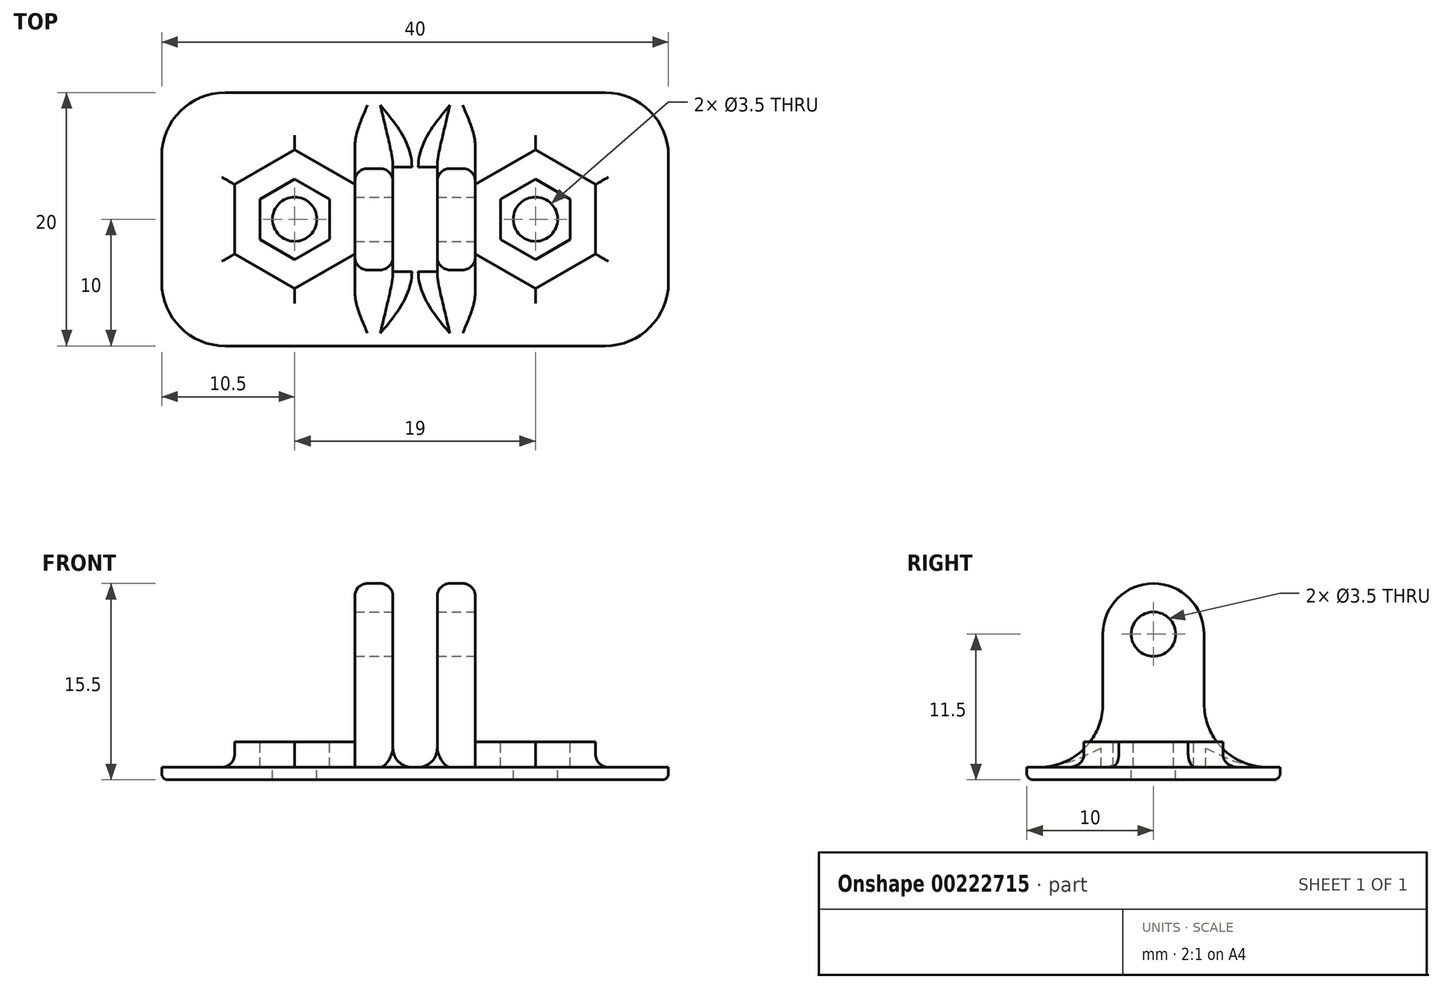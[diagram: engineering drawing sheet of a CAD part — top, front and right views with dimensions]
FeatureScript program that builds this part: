
annotation { "Feature Type Name" : "Feature", "Feature Type Description" : "" }
export const myFeature = defineFeature(function(context is Context, id is Id, definition is map)
    precondition{}
    {
        {
            var Q0;
            Q0=qCreatedBy(makeId("Top.planeOp"),FACE);
            var sketch = newSketch(context, id + "F0", { "sketchPlane" : qUnion([Q0])});
            skLineSegment(sketch, "E0.bottom", {"start": v(0, 0) * mm, "end": v(40, 0) * mm});
            skLineSegment(sketch, "E0.top", {"start": v(0, 20) * mm, "end": v(40, 20) * mm});
            skLineSegment(sketch, "E0.left", {"start": v(0, 0) * mm, "end": v(0, 20) * mm});
            skLineSegment(sketch, "E0.right", {"start": v(40, 0) * mm, "end": v(40, 20) * mm});
            skSolve(sketch);
        }
        {
            var Q0;
            Q0=makeQuery(id+"F0.imprint","IMPRINT",FACE,{"disambiguationData":[TD([[makeQuery(id+"F0.imprint","IMPRINT",EDGE,{"derivedFrom":sQuery(id+"F0.wireOp",EDGE,"E0.bottom")}),1.0]])]});
            extrude(context, id + "F1", {"entities" : qUnion([Q0]), "depth" : 3 * mm});
        }
        {
            var Q0;
            Q0=makeQuery(id+"F1.opExtrude","CAP_FACE",FACE,{"disambiguationData":[OSD([sQuery(id+"F0.wireOp",EDGE,"E0.bottom"),sQuery(id+"F0.wireOp",EDGE,"E0.top"),sQuery(id+"F0.wireOp",EDGE,"E0.left"),sQuery(id+"F0.wireOp",EDGE,"E0.right")])],"isStart":false});
            var sketch = newSketch(context, id + "F2", { "sketchPlane" : qUnion([Q0])});
            skLineSegment(sketch, "E1", {"start": v(20, 20) * mm, "end": v(20, 0) * mm, "construction": true});
            skLineSegment(sketch, "E2.bottom", {"start": v(15.25, 14) * mm, "end": v(18.25, 14) * mm});
            skLineSegment(sketch, "E2.top", {"start": v(15.25, 6) * mm, "end": v(18.25, 6) * mm});
            skLineSegment(sketch, "E2.left", {"start": v(15.25, 14) * mm, "end": v(15.25, 6) * mm});
            skLineSegment(sketch, "E2.right", {"start": v(18.25, 14) * mm, "end": v(18.25, 6) * mm});
            skLineSegment(sketch, "E3", {"start": v(0, 10) * mm, "end": v(40, 10) * mm, "construction": true});
            skLineSegment(sketch, "E4.MirrorCS", {"start": v(24.75, 6) * mm, "end": v(21.75, 6) * mm});
            skLineSegment(sketch, "E5.MirrorCS", {"start": v(40, 10) * mm, "end": v(0, 10) * mm, "construction": true});
            skLineSegment(sketch, "E6.MirrorCS", {"start": v(21.75, 14) * mm, "end": v(21.75, 6) * mm});
            skLineSegment(sketch, "E7.MirrorCS", {"start": v(24.75, 14) * mm, "end": v(24.75, 6) * mm});
            skLineSegment(sketch, "E8.MirrorCS", {"start": v(24.75, 14) * mm, "end": v(21.75, 14) * mm});
            skSolve(sketch);
        }
        {
            var Q0;
            Q0=makeQuery(id+"F2.imprint","IMPRINT",FACE,{"disambiguationData":[TD([[makeQuery(id+"F2.imprint","IMPRINT",EDGE,{"derivedFrom":sQuery(id+"F2.wireOp",EDGE,"E2.bottom")}),-1.0]])]});
            var Q1;
            Q1=makeQuery(id+"F2.imprint","IMPRINT",FACE,{"disambiguationData":[TD([[makeQuery(id+"F2.imprint","IMPRINT",EDGE,{"derivedFrom":sQuery(id+"F2.wireOp",EDGE,"E4.MirrorCS")}),-1.0]])]});
            extrude(context, id + "F3", {"entities" : qUnion([Q0, Q1]), "operationType" : NewBodyOperationType.ADD, "depth" : 12.5 * mm});
        }
        {
            var Q0;
            Q0=makeQuery(id+"F3.opExtrude","SWEPT_FACE",FACE,{"disambiguationData":[OSD([sQuery(id+"F2.wireOp",EDGE,"E7.MirrorCS")])]});
            var sketch = newSketch(context, id + "F4", { "sketchPlane" : qUnion([Q0])});
            skLineSegment(sketch, "E9", {"start": v(10, 15.5) * mm, "end": v(10, 3) * mm, "construction": true});
            skCircle(sketch, "E10", {"center": v(10, 11.5) * mm, "radius": 1.75 * mm});
            skSolve(sketch);
        }
        {
            var Q0;
            Q0=makeQuery(id+"F4.imprint","IMPRINT",FACE,{"disambiguationData":[TD([[makeQuery(id+"F4.imprint","IMPRINT",EDGE,{"derivedFrom":sQuery(id+"F4.wireOp",EDGE,"E10")}),1.0]])]});
            extrude(context, id + "F5", {"entities" : qUnion([Q0]), "operationType" : NewBodyOperationType.REMOVE, "endBound" : BoundingType.THROUGH_ALL, "oppositeDirection" : true, "depth" : 25 * mm});
        }
        {
            var Q0;
            Q0=makeQuery(id+"F1.opExtrude","CAP_FACE",FACE,{"disambiguationData":[OSD([sQuery(id+"F0.wireOp",EDGE,"E0.bottom"),sQuery(id+"F0.wireOp",EDGE,"E0.top"),sQuery(id+"F0.wireOp",EDGE,"E0.left"),sQuery(id+"F0.wireOp",EDGE,"E0.right")])],"isStart":false});
            var sketch = newSketch(context, id + "F6", { "sketchPlane" : qUnion([Q0])});
            skLineSegment(sketch, "E11.0.0", {"start": v(40, 20) * mm, "end": v(0, 20) * mm, "construction": true});
            skLineSegment(sketch, "E11.0.1", {"start": v(0, 20) * mm, "end": v(0, 0) * mm, "construction": true});
            skLineSegment(sketch, "E11.0.2", {"start": v(0, 0) * mm, "end": v(40, 0) * mm, "construction": true});
            skLineSegment(sketch, "E11.0.3", {"start": v(40, 0) * mm, "end": v(40, 20) * mm, "construction": true});
            skLineSegment(sketch, "E12", {"start": v(20, 20) * mm, "end": v(20, 0) * mm, "construction": true});
            skLineSegment(sketch, "E13", {"start": v(0, 10) * mm, "end": v(40.2, 10) * mm, "construction": true});
            skPoint(sketch, "E13.endSnap0", {"position": v(0, 10) * mm});
            skCircle(sketch, "E14.cCircle", {"center": v(20, 10) * mm, "radius": 8.23 * mm, "construction": true});
            skLineSegment(sketch, "E14.0", {"start": v(15.25, 18.23) * mm, "end": v(24.75, 18.23) * mm, "construction": true});
            skLineSegment(sketch, "E14.1", {"start": v(24.75, 18.23) * mm, "end": v(29.5, 10) * mm, "construction": true});
            skLineSegment(sketch, "E14.2", {"start": v(29.5, 10) * mm, "end": v(24.75, 1.77) * mm, "construction": true});
            skLineSegment(sketch, "E14.3", {"start": v(24.75, 1.77) * mm, "end": v(15.25, 1.77) * mm, "construction": true});
            skLineSegment(sketch, "E14.4", {"start": v(15.25, 1.77) * mm, "end": v(10.5, 10) * mm, "construction": true});
            skLineSegment(sketch, "E14.5", {"start": v(10.5, 10) * mm, "end": v(15.25, 18.23) * mm, "construction": true});
            skPoint(sketch, "E14.0.midPoint", {"position": v(20, 18.23) * mm});
            skCircle(sketch, "E15", {"center": v(10.5, 10) * mm, "radius": 1.75 * mm});
            skCircle(sketch, "E16", {"center": v(29.5, 10) * mm, "radius": 1.75 * mm});
            skSolve(sketch);
        }
        {
            var Q0;
            Q0 = qSketchRegion(id + "F6", true);
            extrude(context, id + "F7", {"entities" : qUnion([Q0]), "operationType" : NewBodyOperationType.REMOVE, "endBound" : BoundingType.THROUGH_ALL, "oppositeDirection" : true, "depth" : 25 * mm});
        }
        {
            var Q0;
            Q0=makeQuery(id+"F1.opExtrude","CAP_FACE",FACE,{"disambiguationData":[OSD([sQuery(id+"F0.wireOp",EDGE,"E0.bottom"),sQuery(id+"F0.wireOp",EDGE,"E0.top"),sQuery(id+"F0.wireOp",EDGE,"E0.left"),sQuery(id+"F0.wireOp",EDGE,"E0.right")])],"isStart":false});
            var sketch = newSketch(context, id + "F8", { "sketchPlane" : qUnion([Q0])});
            skCircle(sketch, "E17.cCircle", {"center": v(10.5, 10) * mm, "radius": 2.75 * mm, "construction": true});
            skLineSegment(sketch, "E17.0", {"start": v(13.25, 11.59) * mm, "end": v(13.25, 8.41) * mm});
            skLineSegment(sketch, "E17.1", {"start": v(13.25, 8.41) * mm, "end": v(10.5, 6.82) * mm});
            skLineSegment(sketch, "E17.2", {"start": v(10.5, 6.82) * mm, "end": v(7.75, 8.41) * mm});
            skLineSegment(sketch, "E17.3", {"start": v(7.75, 8.41) * mm, "end": v(7.75, 11.59) * mm});
            skLineSegment(sketch, "E17.4", {"start": v(7.75, 11.59) * mm, "end": v(10.5, 13.18) * mm});
            skLineSegment(sketch, "E17.5", {"start": v(10.5, 13.18) * mm, "end": v(13.25, 11.59) * mm});
            skPoint(sketch, "E17.0.midPoint", {"position": v(13.25, 10) * mm});
            skCircle(sketch, "E18.cCircle", {"center": v(29.5, 10) * mm, "radius": 2.75 * mm, "construction": true});
            skLineSegment(sketch, "E18.0", {"start": v(32.25, 11.59) * mm, "end": v(32.25, 8.41) * mm});
            skLineSegment(sketch, "E18.1", {"start": v(32.25, 8.41) * mm, "end": v(29.5, 6.82) * mm});
            skLineSegment(sketch, "E18.2", {"start": v(29.5, 6.82) * mm, "end": v(26.75, 8.41) * mm});
            skLineSegment(sketch, "E18.3", {"start": v(26.75, 8.41) * mm, "end": v(26.75, 11.59) * mm});
            skLineSegment(sketch, "E18.4", {"start": v(26.75, 11.59) * mm, "end": v(29.5, 13.18) * mm});
            skLineSegment(sketch, "E18.5", {"start": v(29.5, 13.18) * mm, "end": v(32.25, 11.59) * mm});
            skPoint(sketch, "E18.0.midPoint", {"position": v(32.25, 10) * mm});
            skLineSegment(sketch, "E19.0", {"start": v(0, 20) * mm, "end": v(40, 20) * mm});
            skLineSegment(sketch, "E19.1", {"start": v(0, 0) * mm, "end": v(0, 20) * mm});
            skLineSegment(sketch, "E19.2", {"start": v(0, 0) * mm, "end": v(40, 0) * mm});
            skLineSegment(sketch, "E19.3", {"start": v(40, 0) * mm, "end": v(40, 20) * mm});
            skCircle(sketch, "E20.cCircle", {"center": v(10.5, 10) * mm, "radius": 4.75 * mm, "construction": true});
            skPoint(sketch, "E20.cCircle.perimeterSnap0", {"position": v(18.25, 10) * mm});
            skLineSegment(sketch, "E20.0", {"start": v(15.25, 12.74) * mm, "end": v(15.25, 7.26) * mm});
            skLineSegment(sketch, "E20.1", {"start": v(15.25, 7.26) * mm, "end": v(10.5, 4.52) * mm});
            skLineSegment(sketch, "E20.2", {"start": v(10.5, 4.52) * mm, "end": v(5.75, 7.26) * mm});
            skLineSegment(sketch, "E20.3", {"start": v(5.75, 7.26) * mm, "end": v(5.75, 12.74) * mm});
            skLineSegment(sketch, "E20.4", {"start": v(5.75, 12.74) * mm, "end": v(10.5, 15.48) * mm});
            skLineSegment(sketch, "E20.5", {"start": v(10.5, 15.48) * mm, "end": v(15.25, 12.74) * mm});
            skPoint(sketch, "E20.0.midPoint", {"position": v(15.25, 10) * mm});
            skPoint(sketch, "E20.0.midPoint.positionSnap0", {"position": v(18.25, 10) * mm});
            skCircle(sketch, "E21.cCircle", {"center": v(29.5, 10) * mm, "radius": 4.75 * mm, "construction": true});
            skLineSegment(sketch, "E21.0", {"start": v(34.25, 12.74) * mm, "end": v(34.25, 7.26) * mm});
            skLineSegment(sketch, "E21.1", {"start": v(34.25, 7.26) * mm, "end": v(29.5, 4.52) * mm});
            skLineSegment(sketch, "E21.2", {"start": v(29.5, 4.52) * mm, "end": v(24.75, 7.26) * mm});
            skLineSegment(sketch, "E21.3", {"start": v(24.75, 7.26) * mm, "end": v(24.75, 12.74) * mm});
            skLineSegment(sketch, "E21.4", {"start": v(24.75, 12.74) * mm, "end": v(29.5, 15.48) * mm});
            skLineSegment(sketch, "E21.5", {"start": v(29.5, 15.48) * mm, "end": v(34.25, 12.74) * mm});
            skPoint(sketch, "E21.0.midPoint", {"position": v(34.25, 10) * mm});
            skLineSegment(sketch, "E22.0", {"start": v(15.25, 14) * mm, "end": v(15.25, 6) * mm});
            skLineSegment(sketch, "E23.0", {"start": v(24.75, 14) * mm, "end": v(24.75, 6) * mm});
            skSolve(sketch);
        }
        {
            var Q0;
            Q0=makeQuery(id+"F8.imprint","IMPRINT",FACE,{"disambiguationData":[TD([[makeQuery(id+"F8.imprint","IMPRINT",EDGE,{"derivedFrom":sQuery(id+"F8.wireOp",EDGE,"E19.0")}),-1.0]])]});
            var Q1;
            Q1=makeQuery(id+"F8.imprint","IMPRINT",FACE,{"disambiguationData":[TD([[makeQuery(id+"F8.imprint","IMPRINT",EDGE,{"derivedFrom":sQuery(id+"F8.wireOp",EDGE,"E17.0")}),-1.0]])]});
            var Q2;
            Q2=makeQuery(id+"F8.imprint","IMPRINT",FACE,{"disambiguationData":[TD([[makeQuery(id+"F8.imprint","IMPRINT",EDGE,{"derivedFrom":sQuery(id+"F8.wireOp",EDGE,"E18.0")}),-1.0]])]});
            extrude(context, id + "F9", {"entities" : qUnion([Q0, Q1, Q2]), "operationType" : NewBodyOperationType.REMOVE, "oppositeDirection" : true, "depth" : 2 * mm});
        }
        {
            var Q0;
            Q0=makeQuery(id+"F3.opExtrude","CAP_EDGE",EDGE,{"disambiguationData":[OSD([sQuery(id+"F2.wireOp",EDGE,"E4.MirrorCS")])],"isStart":false});
            var Q1;
            Q1=makeQuery(id+"F3.opExtrude","CAP_EDGE",EDGE,{"disambiguationData":[OSD([sQuery(id+"F2.wireOp",EDGE,"E2.top")])],"isStart":false});
            var Q2;
            Q2=makeQuery(id+"F3.opExtrude","CAP_EDGE",EDGE,{"disambiguationData":[OSD([sQuery(id+"F2.wireOp",EDGE,"E2.bottom")])],"isStart":false});
            var Q3;
            Q3=makeQuery(id+"F3.opExtrude","CAP_EDGE",EDGE,{"disambiguationData":[OSD([sQuery(id+"F2.wireOp",EDGE,"E8.MirrorCS")])],"isStart":false});
            fillet(context, id + "F10", {"entities" : qUnion([Q0, Q1, Q2, Q3]), "radius" : 4 * mm, "tangentPropagation" : true, "allowEdgeOverflow" : false});
        }
        {
            var Q0;
            Q0=makeQuery(id+"F1.opExtrude","SWEPT_EDGE",EDGE,{"disambiguationData":[OSD([sQuery(id+"F0.wireOp",EDGE,"E0.top"),sQuery(id+"F0.wireOp",EDGE,"E0.left")])]});
            var Q1;
            Q1=makeQuery(id+"F1.opExtrude","SWEPT_EDGE",EDGE,{"disambiguationData":[OSD([sQuery(id+"F0.wireOp",EDGE,"E0.bottom"),sQuery(id+"F0.wireOp",EDGE,"E0.left")])]});
            var Q2;
            Q2=makeQuery(id+"F1.opExtrude","SWEPT_EDGE",EDGE,{"disambiguationData":[OSD([sQuery(id+"F0.wireOp",EDGE,"E0.bottom"),sQuery(id+"F0.wireOp",EDGE,"E0.right")])]});
            var Q3;
            Q3=makeQuery(id+"F1.opExtrude","SWEPT_EDGE",EDGE,{"disambiguationData":[OSD([sQuery(id+"F0.wireOp",EDGE,"E0.top"),sQuery(id+"F0.wireOp",EDGE,"E0.right")])]});
            fillet(context, id + "F11", {"entities" : qUnion([Q0, Q1, Q2, Q3]), "radius" : 5 * mm, "tangentPropagation" : true, "allowEdgeOverflow" : false});
        }
        {
            var Q0;
            Q0=makeQuery(id+"F9.boolean.opBoolean","COPY",EDGE,{"derivedFrom":makeQuery(id+"F9.opExtrude","CAP_EDGE",EDGE,{"disambiguationData":[OSD([sQuery(id+"F8.wireOp",EDGE,"E19.0")])],"isStart":false})});
            var Q1;
            Q1=makeQuery(id+"F1.opExtrude","CAP_EDGE",EDGE,{"disambiguationData":[OSD([sQuery(id+"F0.wireOp",EDGE,"E0.top")])],"isStart":true});
            fillet(context, id + "F12", {"entities" : qUnion([Q0, Q1]), "radius" : 0.5 * mm, "tangentPropagation" : true, "allowEdgeOverflow" : false});
        }
        {
            var Q0;
            Q0=makeQuery(id+"F9.boolean.opBoolean","COPY",EDGE,{"derivedFrom":makeQuery(id+"F9.opExtrude","CAP_EDGE",EDGE,{"disambiguationData":[OSD([sQuery(id+"F8.wireOp",EDGE,"E20.5")])],"isStart":false})});
            var Q1;
            Q1=makeQuery(id+"F9.boolean.opBoolean","COPY",EDGE,{"derivedFrom":makeQuery(id+"F9.opExtrude","CAP_EDGE",EDGE,{"disambiguationData":[OSD([sQuery(id+"F8.wireOp",EDGE,"E20.4")])],"isStart":false})});
            var Q2;
            Q2=makeQuery(id+"F9.boolean.opBoolean","COPY",EDGE,{"derivedFrom":makeQuery(id+"F9.opExtrude","CAP_EDGE",EDGE,{"disambiguationData":[OSD([sQuery(id+"F8.wireOp",EDGE,"E21.4")])],"isStart":false})});
            var Q3;
            Q3=makeQuery(id+"F9.boolean.opBoolean","COPY",EDGE,{"derivedFrom":makeQuery(id+"F9.opExtrude","CAP_EDGE",EDGE,{"disambiguationData":[OSD([sQuery(id+"F8.wireOp",EDGE,"E21.5")])],"isStart":false})});
            var Q4;
            Q4=makeQuery(id+"F9.boolean.opBoolean","COPY",EDGE,{"derivedFrom":makeQuery(id+"F9.opExtrude","CAP_EDGE",EDGE,{"disambiguationData":[OSD([sQuery(id+"F8.wireOp",EDGE,"E21.0")])],"isStart":false})});
            var Q5;
            Q5=makeQuery(id+"F9.boolean.opBoolean","COPY",EDGE,{"derivedFrom":makeQuery(id+"F9.opExtrude","CAP_EDGE",EDGE,{"disambiguationData":[OSD([sQuery(id+"F8.wireOp",EDGE,"E21.1")])],"isStart":false})});
            var Q6;
            Q6=makeQuery(id+"F9.boolean.opBoolean","COPY",EDGE,{"derivedFrom":makeQuery(id+"F9.opExtrude","CAP_EDGE",EDGE,{"disambiguationData":[OSD([sQuery(id+"F8.wireOp",EDGE,"E21.2")])],"isStart":false})});
            var Q7;
            Q7=makeQuery(id+"F9.boolean.opBoolean","COPY",EDGE,{"derivedFrom":makeQuery(id+"F9.opExtrude","CAP_EDGE",EDGE,{"disambiguationData":[OSD([sQuery(id+"F8.wireOp",EDGE,"E20.1")])],"isStart":false})});
            var Q8;
            Q8=makeQuery(id+"F9.boolean.opBoolean","COPY",EDGE,{"derivedFrom":makeQuery(id+"F9.opExtrude","CAP_EDGE",EDGE,{"disambiguationData":[OSD([sQuery(id+"F8.wireOp",EDGE,"E20.2")])],"isStart":false})});
            var Q9;
            Q9=makeQuery(id+"F9.boolean.opBoolean","COPY",EDGE,{"derivedFrom":makeQuery(id+"F9.opExtrude","CAP_EDGE",EDGE,{"disambiguationData":[OSD([sQuery(id+"F8.wireOp",EDGE,"E20.3")])],"isStart":false})});
            fillet(context, id + "F13", {"entities" : qUnion([Q0, Q1, Q2, Q3, Q4, Q5, Q6, Q7, Q8, Q9]), "radius" : 1 * mm, "tangentPropagation" : true, "allowEdgeOverflow" : false});
        }
        {
            var Q0;
            Q0=makeQuery(id+"F9.boolean.opBoolean","COPY",EDGE,{"derivedFrom":makeQuery(id+"F9.opExtrude","CAP_EDGE",EDGE,{"disambiguationData":[OSD([sQuery(id+"F2.wireOp",EDGE,"E2.bottom")])],"isStart":false})});
            var Q1;
            Q1=makeQuery(id+"F9.boolean.opBoolean","COPY",EDGE,{"derivedFrom":makeQuery(id+"F9.opExtrude","CAP_EDGE",EDGE,{"disambiguationData":[OSD([sQuery(id+"F2.wireOp",EDGE,"E8.MirrorCS")])],"isStart":false})});
            var Q2;
            Q2=makeQuery(id+"F9.boolean.opBoolean","COPY",EDGE,{"derivedFrom":makeQuery(id+"F9.opExtrude","CAP_EDGE",EDGE,{"disambiguationData":[OSD([sQuery(id+"F2.wireOp",EDGE,"E2.top")])],"isStart":false})});
            var Q3;
            Q3=makeQuery(id+"F9.boolean.opBoolean","COPY",EDGE,{"derivedFrom":makeQuery(id+"F9.opExtrude","CAP_EDGE",EDGE,{"disambiguationData":[OSD([sQuery(id+"F2.wireOp",EDGE,"E4.MirrorCS")])],"isStart":false})});
            fillet(context, id + "F14", {"entities" : qUnion([Q0, Q1, Q2, Q3]), "radius" : 5 * mm, "tangentPropagation" : true, "allowEdgeOverflow" : false});
        }
        {
            var Q0;
            {var subQ0=sQuery(id+"F2.wireOp",EDGE,"E2.right");Q0=makeQuery(id+"F14.opFillet","BLEND_EDGE",EDGE,{"blendedFrom":[makeQuery(id+"F9.boolean.opBoolean","COPY",EDGE,{"derivedFrom":makeQuery(id+"F9.opExtrude","CAP_EDGE",EDGE,{"disambiguationData":[OSD([sQuery(id+"F2.wireOp",EDGE,"E2.top")])],"isStart":false})}),makeQuery(id+"F9.boolean.opBoolean","MERGE",FACE,{"derivedFrom":[makeQuery(id+"F3.opExtrude","SWEPT_FACE",FACE,{"disambiguationData":[OSD([subQ0])]}),makeQuery(id+"F9.opExtrude","SWEPT_FACE",FACE,{"disambiguationData":[OSD([subQ0])]})]})],"blendedInto":[makeQuery(id+"F9.boolean.opBoolean","MERGE",FACE,{"derivedFrom":[makeQuery(id+"F3.opExtrude","SWEPT_FACE",FACE,{"disambiguationData":[OSD([subQ0])]}),makeQuery(id+"F9.opExtrude","SWEPT_FACE",FACE,{"disambiguationData":[OSD([subQ0])]})]})]});}
            var Q1;
            {var subQ0=sQuery(id+"F8.wireOp",EDGE,"E22.0");var subQ1=sQuery(id+"F2.wireOp",EDGE,"E2.top");Q1=makeQuery(id+"F14.opFillet","BLEND_EDGE",EDGE,{"blendedFrom":[makeQuery(id+"F9.boolean.opBoolean","COPY",EDGE,{"derivedFrom":makeQuery(id+"F9.opExtrude","CAP_EDGE",EDGE,{"disambiguationData":[OSD([subQ1])],"isStart":false})}),makeQuery(id+"F9.boolean.opBoolean","MERGE",FACE,{"derivedFrom":[makeQuery(id+"F3.opExtrude","SWEPT_FACE",FACE,{"disambiguationData":[OSD([sQuery(id+"F2.wireOp",EDGE,"E2.left")])]}),makeQuery(id+"F9.opExtrude","SWEPT_FACE",FACE,{"disambiguationData":[OSD([subQ0]),TDD([makeQuery(id+"F8.imprint","IMPRINT",EDGE,{"disambiguationData":[TD([[makeQuery(id+"F8.imprint","INTERSECT",VERTEX,{"derivedFrom":[makeQuery(id+"F3.opExtrude","CAP_EDGE",EDGE,{"disambiguationData":[OSD([sQuery(id+"F2.wireOp",EDGE,"E2.bottom")])],"isStart":true}),subQ0]}),-1.0]])],"derivedFrom":subQ0})])]}),makeQuery(id+"F9.opExtrude","SWEPT_FACE",FACE,{"disambiguationData":[OSD([subQ0]),TDD([makeQuery(id+"F8.imprint","IMPRINT",EDGE,{"disambiguationData":[TD([[makeQuery(id+"F8.imprint","INTERSECT",VERTEX,{"derivedFrom":[makeQuery(id+"F3.opExtrude","CAP_EDGE",EDGE,{"disambiguationData":[OSD([subQ1])],"isStart":true}),subQ0]}),1.0]])],"derivedFrom":subQ0})])]})]})],"blendedInto":[makeQuery(id+"F9.boolean.opBoolean","MERGE",FACE,{"derivedFrom":[makeQuery(id+"F3.opExtrude","SWEPT_FACE",FACE,{"disambiguationData":[OSD([sQuery(id+"F2.wireOp",EDGE,"E2.left")])]}),makeQuery(id+"F9.opExtrude","SWEPT_FACE",FACE,{"disambiguationData":[OSD([subQ0]),TDD([makeQuery(id+"F8.imprint","IMPRINT",EDGE,{"disambiguationData":[TD([[makeQuery(id+"F8.imprint","INTERSECT",VERTEX,{"derivedFrom":[makeQuery(id+"F3.opExtrude","CAP_EDGE",EDGE,{"disambiguationData":[OSD([sQuery(id+"F2.wireOp",EDGE,"E2.bottom")])],"isStart":true}),subQ0]}),-1.0]])],"derivedFrom":subQ0})])]}),makeQuery(id+"F9.opExtrude","SWEPT_FACE",FACE,{"disambiguationData":[OSD([subQ0]),TDD([makeQuery(id+"F8.imprint","IMPRINT",EDGE,{"disambiguationData":[TD([[makeQuery(id+"F8.imprint","INTERSECT",VERTEX,{"derivedFrom":[makeQuery(id+"F3.opExtrude","CAP_EDGE",EDGE,{"disambiguationData":[OSD([subQ1])],"isStart":true}),subQ0]}),1.0]])],"derivedFrom":subQ0})])]})]})]});}
            var Q2;
            {var subQ0=sQuery(id+"F2.wireOp",EDGE,"E6.MirrorCS");Q2=makeQuery(id+"F14.opFillet","BLEND_EDGE",EDGE,{"blendedFrom":[makeQuery(id+"F9.boolean.opBoolean","COPY",EDGE,{"derivedFrom":makeQuery(id+"F9.opExtrude","CAP_EDGE",EDGE,{"disambiguationData":[OSD([sQuery(id+"F2.wireOp",EDGE,"E8.MirrorCS")])],"isStart":false})}),makeQuery(id+"F9.boolean.opBoolean","MERGE",FACE,{"derivedFrom":[makeQuery(id+"F3.opExtrude","SWEPT_FACE",FACE,{"disambiguationData":[OSD([subQ0])]}),makeQuery(id+"F9.opExtrude","SWEPT_FACE",FACE,{"disambiguationData":[OSD([subQ0])]})]})],"blendedInto":[makeQuery(id+"F9.boolean.opBoolean","MERGE",FACE,{"derivedFrom":[makeQuery(id+"F3.opExtrude","SWEPT_FACE",FACE,{"disambiguationData":[OSD([subQ0])]}),makeQuery(id+"F9.opExtrude","SWEPT_FACE",FACE,{"disambiguationData":[OSD([subQ0])]})]})]});}
            var Q3;
            {var subQ0=sQuery(id+"F8.wireOp",EDGE,"E23.0");var subQ1=sQuery(id+"F2.wireOp",EDGE,"E8.MirrorCS");Q3=makeQuery(id+"F14.opFillet","BLEND_EDGE",EDGE,{"blendedFrom":[makeQuery(id+"F9.boolean.opBoolean","COPY",EDGE,{"derivedFrom":makeQuery(id+"F9.opExtrude","CAP_EDGE",EDGE,{"disambiguationData":[OSD([subQ1])],"isStart":false})}),makeQuery(id+"F9.boolean.opBoolean","MERGE",FACE,{"derivedFrom":[makeQuery(id+"F3.opExtrude","SWEPT_FACE",FACE,{"disambiguationData":[OSD([sQuery(id+"F2.wireOp",EDGE,"E7.MirrorCS")])]}),makeQuery(id+"F9.opExtrude","SWEPT_FACE",FACE,{"disambiguationData":[OSD([subQ0]),TDD([makeQuery(id+"F8.imprint","IMPRINT",EDGE,{"disambiguationData":[TD([[makeQuery(id+"F8.imprint","INTERSECT",VERTEX,{"derivedFrom":[makeQuery(id+"F3.opExtrude","CAP_EDGE",EDGE,{"disambiguationData":[OSD([subQ1])],"isStart":true}),subQ0]}),-1.0]])],"derivedFrom":subQ0})])]}),makeQuery(id+"F9.opExtrude","SWEPT_FACE",FACE,{"disambiguationData":[OSD([subQ0]),TDD([makeQuery(id+"F8.imprint","IMPRINT",EDGE,{"disambiguationData":[TD([[makeQuery(id+"F8.imprint","INTERSECT",VERTEX,{"derivedFrom":[makeQuery(id+"F3.opExtrude","CAP_EDGE",EDGE,{"disambiguationData":[OSD([sQuery(id+"F2.wireOp",EDGE,"E4.MirrorCS")])],"isStart":true}),subQ0]}),1.0]])],"derivedFrom":subQ0})])]})]})],"blendedInto":[makeQuery(id+"F9.boolean.opBoolean","MERGE",FACE,{"derivedFrom":[makeQuery(id+"F3.opExtrude","SWEPT_FACE",FACE,{"disambiguationData":[OSD([sQuery(id+"F2.wireOp",EDGE,"E7.MirrorCS")])]}),makeQuery(id+"F9.opExtrude","SWEPT_FACE",FACE,{"disambiguationData":[OSD([subQ0]),TDD([makeQuery(id+"F8.imprint","IMPRINT",EDGE,{"disambiguationData":[TD([[makeQuery(id+"F8.imprint","INTERSECT",VERTEX,{"derivedFrom":[makeQuery(id+"F3.opExtrude","CAP_EDGE",EDGE,{"disambiguationData":[OSD([subQ1])],"isStart":true}),subQ0]}),-1.0]])],"derivedFrom":subQ0})])]}),makeQuery(id+"F9.opExtrude","SWEPT_FACE",FACE,{"disambiguationData":[OSD([subQ0]),TDD([makeQuery(id+"F8.imprint","IMPRINT",EDGE,{"disambiguationData":[TD([[makeQuery(id+"F8.imprint","INTERSECT",VERTEX,{"derivedFrom":[makeQuery(id+"F3.opExtrude","CAP_EDGE",EDGE,{"disambiguationData":[OSD([sQuery(id+"F2.wireOp",EDGE,"E4.MirrorCS")])],"isStart":true}),subQ0]}),1.0]])],"derivedFrom":subQ0})])]})]})]});}
            fillet(context, id + "F15", {"entities" : qUnion([Q0, Q1, Q2, Q3]), "radius" : 1 * mm, "tangentPropagation" : true, "allowEdgeOverflow" : false});
        }
        {
            var Q0;
            Q0=makeQuery(id+"F9.boolean.opBoolean","COPY",EDGE,{"derivedFrom":makeQuery(id+"F9.opExtrude","CAP_EDGE",EDGE,{"disambiguationData":[OSD([sQuery(id+"F2.wireOp",EDGE,"E2.right")])],"isStart":false})});
            var Q1;
            Q1=makeQuery(id+"F9.boolean.opBoolean","COPY",EDGE,{"derivedFrom":makeQuery(id+"F9.opExtrude","CAP_EDGE",EDGE,{"disambiguationData":[OSD([sQuery(id+"F2.wireOp",EDGE,"E6.MirrorCS")])],"isStart":false})});
            fillet(context, id + "F16", {"entities" : qUnion([Q0, Q1]), "radius" : 1.5 * mm, "tangentPropagation" : true, "allowEdgeOverflow" : false});
        }
    });
